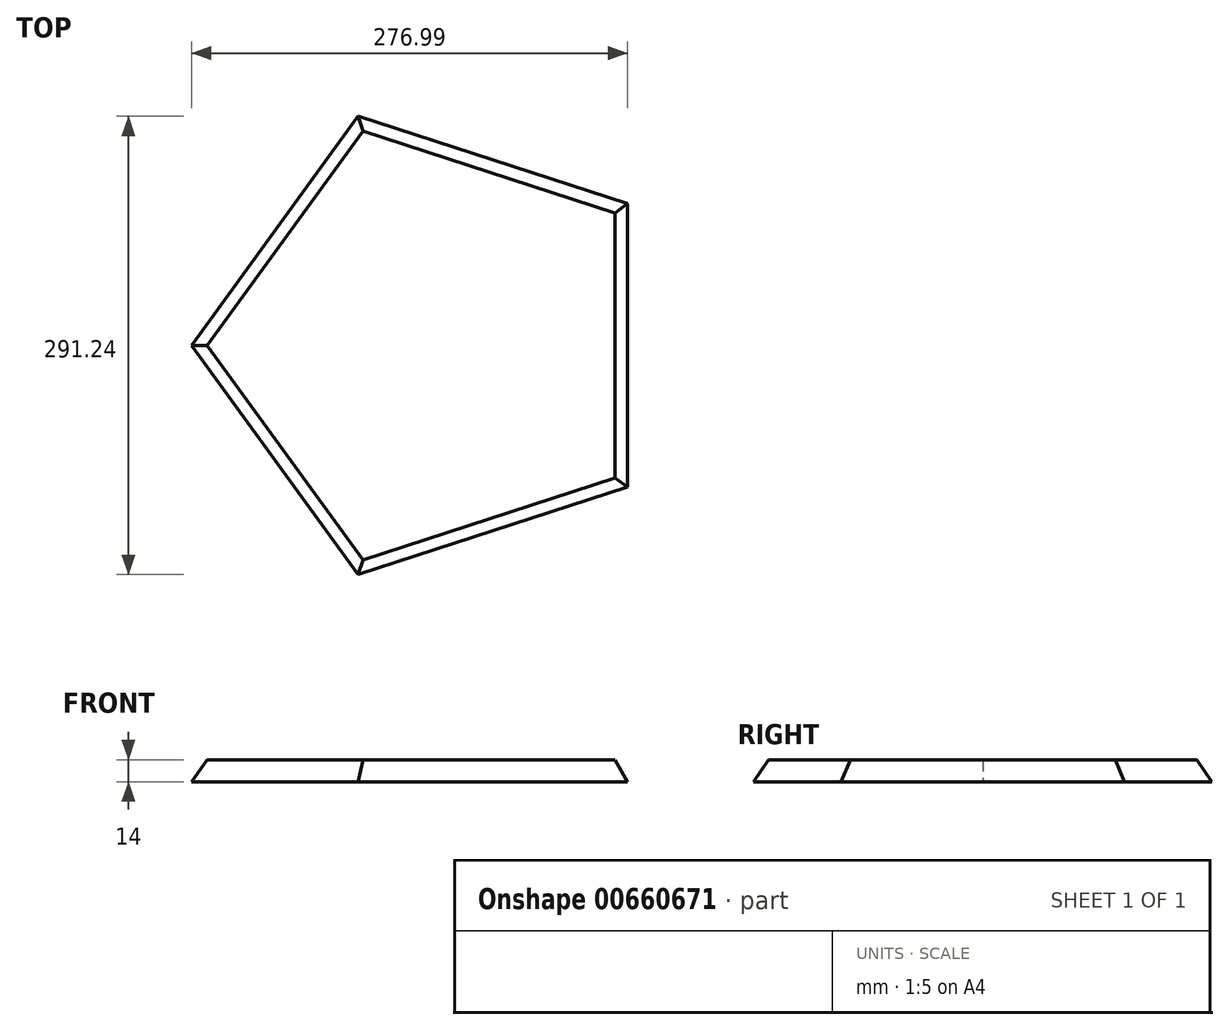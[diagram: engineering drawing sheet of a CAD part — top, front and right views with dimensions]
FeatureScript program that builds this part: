
annotation { "Feature Type Name" : "Feature", "Feature Type Description" : "" }
export const myFeature = defineFeature(function(context is Context, id is Id, definition is map)
    precondition{}
    {
        {
            var Q0;
            Q0=qCreatedBy(makeId("Top.planeOp"),FACE);
            var sketch = newSketch(context, id + "F0", { "sketchPlane" : qUnion([Q0])});
            skCircle(sketch, "E0.cCircle", {"center": v(0, 0) * mm, "radius": 123.87 * mm, "construction": true});
            skLineSegment(sketch, "E0.0", {"start": v(123.87, 90) * mm, "end": v(123.87, -90) * mm});
            skLineSegment(sketch, "E0.1", {"start": v(123.87, -90) * mm, "end": v(-47.32, -145.62) * mm});
            skLineSegment(sketch, "E0.2", {"start": v(-47.32, -145.62) * mm, "end": v(-153.12, 0) * mm});
            skLineSegment(sketch, "E0.3", {"start": v(-153.12, 0) * mm, "end": v(-47.32, 145.62) * mm});
            skLineSegment(sketch, "E0.4", {"start": v(-47.32, 145.62) * mm, "end": v(123.87, 90) * mm});
            skPoint(sketch, "E0.0.midPoint", {"position": v(123.87, 0) * mm});
            skSolve(sketch);
        }
        {
            var Q0;
            Q0 = qSketchRegion(id + "F0", true);
            extrude(context, id + "F1", {"entities" : qUnion([Q0]), "depth" : 14 * mm, "offsetDistance" : 25 * mm});
        }
        {
            var Q0;
            Q0=makeQuery(id+"F1.opExtrude","CAP_FACE",FACE,{"disambiguationData":[OSD([sQuery(id+"F0.wireOp",EDGE,"E0.0"),sQuery(id+"F0.wireOp",EDGE,"E0.1"),sQuery(id+"F0.wireOp",EDGE,"E0.2"),sQuery(id+"F0.wireOp",EDGE,"E0.3"),sQuery(id+"F0.wireOp",EDGE,"E0.4")])],"isStart":false});
            chamfer(context, id + "F2", {"entities" : qUnion([Q0]), "chamferType" : ChamferType.OFFSET_ANGLE, "width" : 14 * mm, "oppositeDirection" : false, "angle" : 30 * degree, "tangentPropagation" : true});
        }
        {
            var Q0;
            Q0=makeQuery(id+"F1.opExtrude","SWEPT_BODY",BODY,{"disambiguationData":[OSD([sQuery(id+"F0.wireOp",EDGE,"E0.0"),sQuery(id+"F0.wireOp",EDGE,"E0.1"),sQuery(id+"F0.wireOp",EDGE,"E0.2"),sQuery(id+"F0.wireOp",EDGE,"E0.3"),sQuery(id+"F0.wireOp",EDGE,"E0.4")])]});
            transform(context, id + "F3", {"entities" : qUnion([Q0]), "transformType" : TransformType.TRANSLATION_3D, "dx" : 0 * mm, "dy" : 0 * mm, "dz" : 0 * mm, "makeCopy" : true});
        }
        {
            var Q0;
            Q0=makeQuery(id+"F3.opPattern","COPY",BODY,{"derivedFrom":makeQuery(id+"F1.opExtrude","SWEPT_BODY",BODY,{"disambiguationData":[OSD([sQuery(id+"F0.wireOp",EDGE,"E0.0"),sQuery(id+"F0.wireOp",EDGE,"E0.1"),sQuery(id+"F0.wireOp",EDGE,"E0.2"),sQuery(id+"F0.wireOp",EDGE,"E0.3"),sQuery(id+"F0.wireOp",EDGE,"E0.4")])]}),"instanceName":"1"});
            deleteBodies(context, id + "F4", {"entities" : qUnion([Q0])});
        }
        {
            var Q0;
            Q0=makeQuery(id+"F1.opExtrude","SWEPT_BODY",BODY,{"disambiguationData":[OSD([sQuery(id+"F0.wireOp",EDGE,"E0.0"),sQuery(id+"F0.wireOp",EDGE,"E0.1"),sQuery(id+"F0.wireOp",EDGE,"E0.2"),sQuery(id+"F0.wireOp",EDGE,"E0.3"),sQuery(id+"F0.wireOp",EDGE,"E0.4")])]});
            transform(context, id + "F5", {"entities" : qUnion([Q0]), "transformType" : TransformType.TRANSLATION_3D, "dx" : 14 * mm, "dy" : 14 * mm, "dz" : 14 * mm, "makeCopy" : true});
        }
        {
            var Q0;
            Q0=makeQuery(id+"F5.opPattern","COPY",BODY,{"derivedFrom":makeQuery(id+"F1.opExtrude","SWEPT_BODY",BODY,{"disambiguationData":[OSD([sQuery(id+"F0.wireOp",EDGE,"E0.0"),sQuery(id+"F0.wireOp",EDGE,"E0.1"),sQuery(id+"F0.wireOp",EDGE,"E0.2"),sQuery(id+"F0.wireOp",EDGE,"E0.3"),sQuery(id+"F0.wireOp",EDGE,"E0.4")])]}),"instanceName":"1"});
            deleteBodies(context, id + "F6", {"entities" : qUnion([Q0])});
        }
    });
